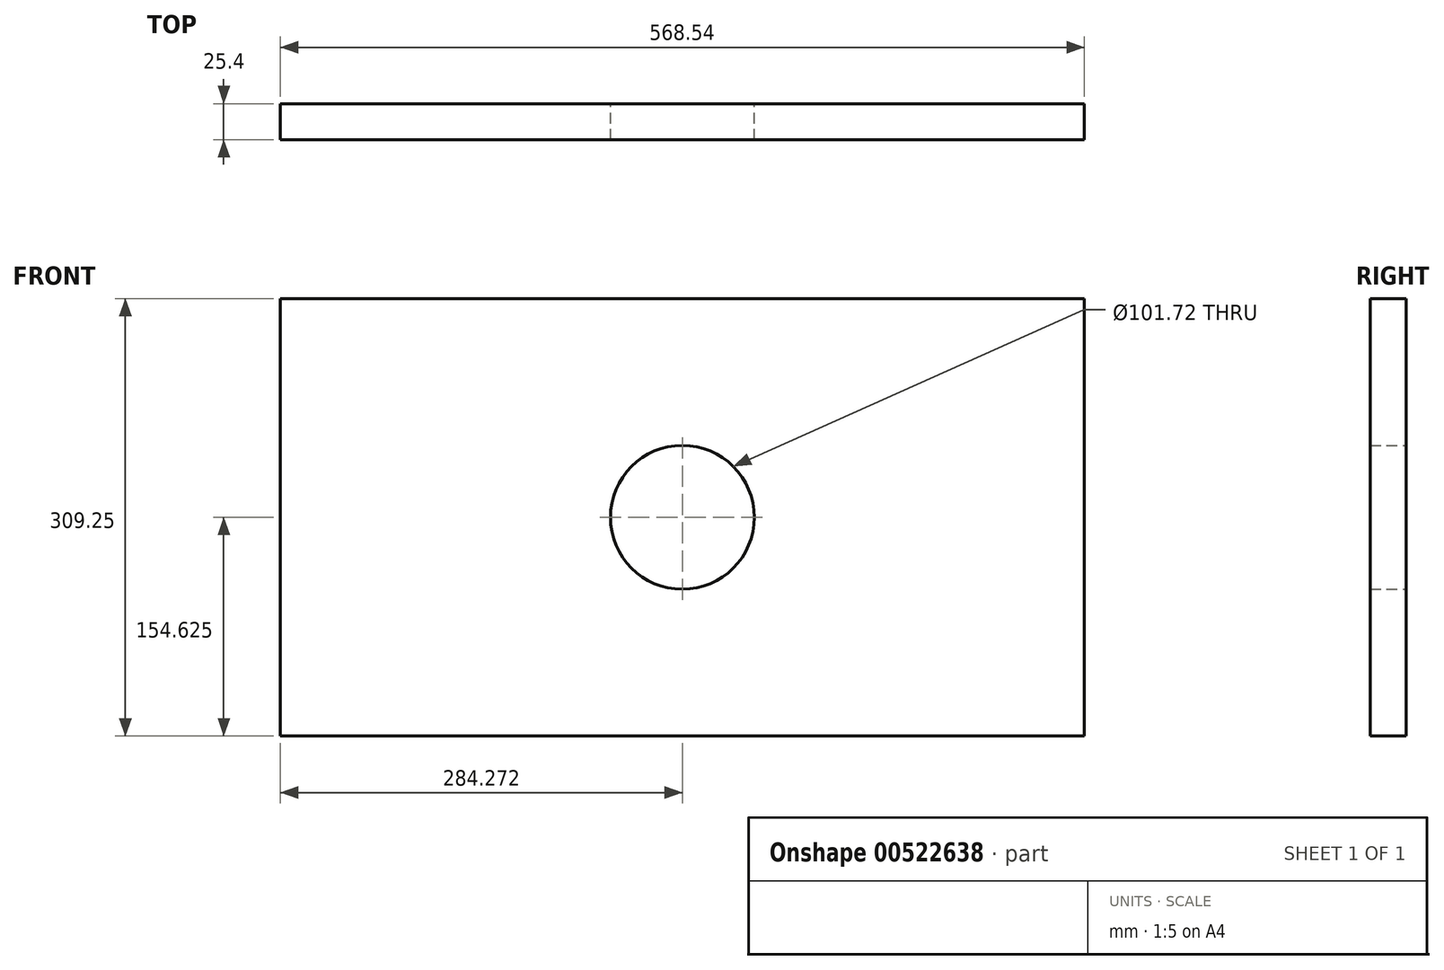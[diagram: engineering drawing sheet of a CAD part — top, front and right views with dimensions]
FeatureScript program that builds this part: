
annotation { "Feature Type Name" : "Feature", "Feature Type Description" : "" }
export const myFeature = defineFeature(function(context is Context, id is Id, definition is map)
    precondition{}
    {
        {
            var Q0;
            Q0=qCreatedBy(makeId("Front.planeOp"),FACE);
            var sketch = newSketch(context, id + "F0", { "sketchPlane" : qUnion([Q0])});
            skLineSegment(sketch, "E0.bottom", {"start": v(216.25, -78.14) * mm, "end": v(-352.29, -78.14) * mm});
            skLineSegment(sketch, "E0.top", {"start": v(216.25, 231.1) * mm, "end": v(-352.29, 231.1) * mm});
            skLineSegment(sketch, "E0.left", {"start": v(216.25, -78.14) * mm, "end": v(216.25, 231.1) * mm});
            skLineSegment(sketch, "E0.right", {"start": v(-352.29, -78.14) * mm, "end": v(-352.29, 231.1) * mm});
            skPoint(sketch, "E0.middle", {"position": v(-68.02, 76.49) * mm});
            skLineSegment(sketch, "E1", {"start": v(-352.29, 76.49) * mm, "end": v(216.25, 76.49) * mm});
            skLineSegment(sketch, "E2", {"start": v(-68.02, 231.1) * mm, "end": v(-68.02, -78.14) * mm});
            skCircle(sketch, "E3", {"center": v(-68.02, 76.49) * mm, "radius": 50.86 * mm});
            skSolve(sketch);
        }
        {
            var Q0;
            Q0 = qSketchRegion(id + "F0", true);
            extrude(context, id + "F1", {"entities" : qUnion([Q0]), "depth" : 25.4 * mm, "offsetDistance" : 25.4 * mm});
        }
    });
